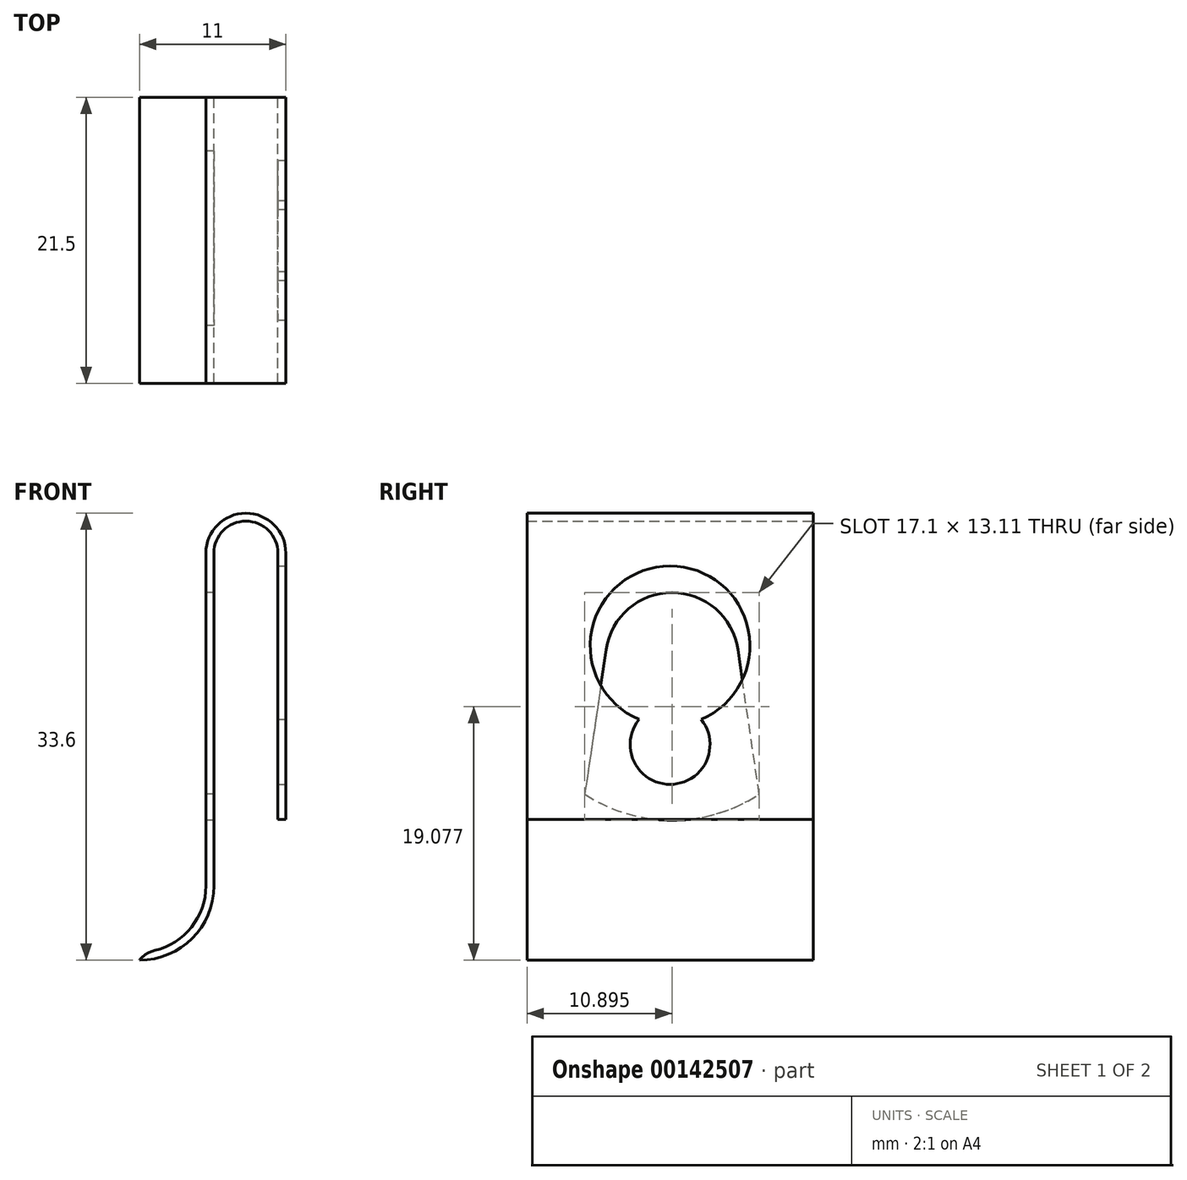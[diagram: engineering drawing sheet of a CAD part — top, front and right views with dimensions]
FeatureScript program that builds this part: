
annotation { "Feature Type Name" : "Feature", "Feature Type Description" : "" }
export const myFeature = defineFeature(function(context is Context, id is Id, definition is map)
    precondition{}
    {
        {
            var Q0;
            Q0=qCreatedBy(makeId("Front.planeOp"),FACE);
            var sketch = newSketch(context, id + "F0", { "sketchPlane" : qUnion([Q0])});
            skLineSegment(sketch, "E0", {"start": v(0, 0) * mm, "end": v(0, 25) * mm});
            skLineSegment(sketch, "E1", {"start": v(6, 25) * mm, "end": v(6, 5) * mm});
            skArc(sketch, "E2", {"start": v(6, 25) * mm, "mid": v(3, 28) * mm, "end": v(0, 25) * mm});
            skArc(sketch, "E3", {"start": v(-5, -5) * mm, "mid": v(-1.46, -3.54) * mm, "end": v(0, 0) * mm});
            skLineSegment(sketch, "E4.0", {"start": v(5.4, 25) * mm, "end": v(5.4, 5) * mm});
            skArc(sketch, "E4.1", {"start": v(5.4, 25) * mm, "mid": v(3, 27.4) * mm, "end": v(0.6, 25) * mm});
            skLineSegment(sketch, "E4.2", {"start": v(0.6, 0) * mm, "end": v(0.6, 25) * mm});
            skArc(sketch, "E4.3", {"start": v(-5, -5.6) * mm, "mid": v(-1.04, -3.96) * mm, "end": v(0.6, 0) * mm});
            skLineSegment(sketch, "E5", {"start": v(-5, -5.6) * mm, "end": v(-5, -5) * mm});
            skLineSegment(sketch, "E6", {"start": v(5.4, 5) * mm, "end": v(6, 5) * mm});
            skSolve(sketch);
        }
        {
            var Q0;
            Q0=makeQuery(id+"F0.imprint","IMPRINT",FACE,{"disambiguationData":[TD([[makeQuery(id+"F0.imprint","IMPRINT",EDGE,{"derivedFrom":sQuery(id+"F0.wireOp",EDGE,"E0")}),-1.0]])]});
            extrude(context, id + "F1", {"entities" : qUnion([Q0]), "depth" : 21.5 * mm});
        }
        {
            var Q0;
            Q0=makeQuery(id+"F1.opExtrude","SWEPT_FACE",FACE,{"disambiguationData":[OSD([sQuery(id+"F0.wireOp",EDGE,"E0")])]});
            var sketch = newSketch(context, id + "F2", { "sketchPlane" : qUnion([Q0])});
            skLineSegment(sketch, "E7", {"start": v(4.05, 6.88) * mm, "end": v(5.66, 17.76) * mm});
            skLineSegment(sketch, "E8", {"start": v(15.55, 17.76) * mm, "end": v(17.16, 6.88) * mm});
            skArc(sketch, "E9", {"start": v(15.55, 17.76) * mm, "mid": v(10.6, 22.03) * mm, "end": v(5.66, 17.76) * mm});
            skArc(sketch, "E10", {"start": v(4.05, 6.88) * mm, "mid": v(10.6, 4.93) * mm, "end": v(17.16, 6.88) * mm});
            skSolve(sketch);
        }
        {
            var Q0;
            Q0=makeQuery(id+"F2.imprint","IMPRINT",FACE,{"disambiguationData":[TD([[makeQuery(id+"F2.imprint","IMPRINT",EDGE,{"derivedFrom":sQuery(id+"F2.wireOp",EDGE,"E7")}),-1.0]])]});
            extrude(context, id + "F3", {"entities" : qUnion([Q0]), "operationType" : NewBodyOperationType.REMOVE, "oppositeDirection" : true, "depth" : 1.8 * mm});
        }
        {
            var Q0;
            Q0=makeQuery(id+"F1.opExtrude","SWEPT_FACE",FACE,{"disambiguationData":[OSD([sQuery(id+"F0.wireOp",EDGE,"E1")])]});
            var sketch = newSketch(context, id + "F4", { "sketchPlane" : qUnion([Q0])});
            skArc(sketch, "E11", {"start": v(-8.42, 12.5) * mm, "mid": v(-10.75, 24.03) * mm, "end": v(-13.08, 12.5) * mm});
            skArc(sketch, "E12", {"start": v(-13.08, 12.5) * mm, "mid": v(-10.75, 7.62) * mm, "end": v(-8.42, 12.5) * mm});
            skSolve(sketch);
        }
        {
            var Q0;
            Q0 = qSketchRegion(id + "F4", true);
            var Q1;
            Q1=makeQuery(id+"F4.imprint","IMPRINT",FACE,{"disambiguationData":[TD([[makeQuery(id+"F4.imprint","IMPRINT",EDGE,{"derivedFrom":sQuery(id+"F4.wireOp",EDGE,"E11")}),1.0]])]});
            extrude(context, id + "F5", {"entities" : qUnion([Q0, Q1]), "operationType" : NewBodyOperationType.REMOVE, "oppositeDirection" : true, "depth" : 2.46 * mm});
        }
        {
            var Q0;
            Q0=makeQuery(id+"F1.opExtrude","SWEPT_EDGE",EDGE,{"disambiguationData":[OSD([sQuery(id+"F0.wireOp",EDGE,"E3"),sQuery(id+"F0.wireOp",EDGE,"E5")])]});
            fillet(context, id + "F6", {"entities" : qUnion([Q0]), "radius" : 2 * mm, "tangentPropagation" : true, "allowEdgeOverflow" : false});
        }
    });
